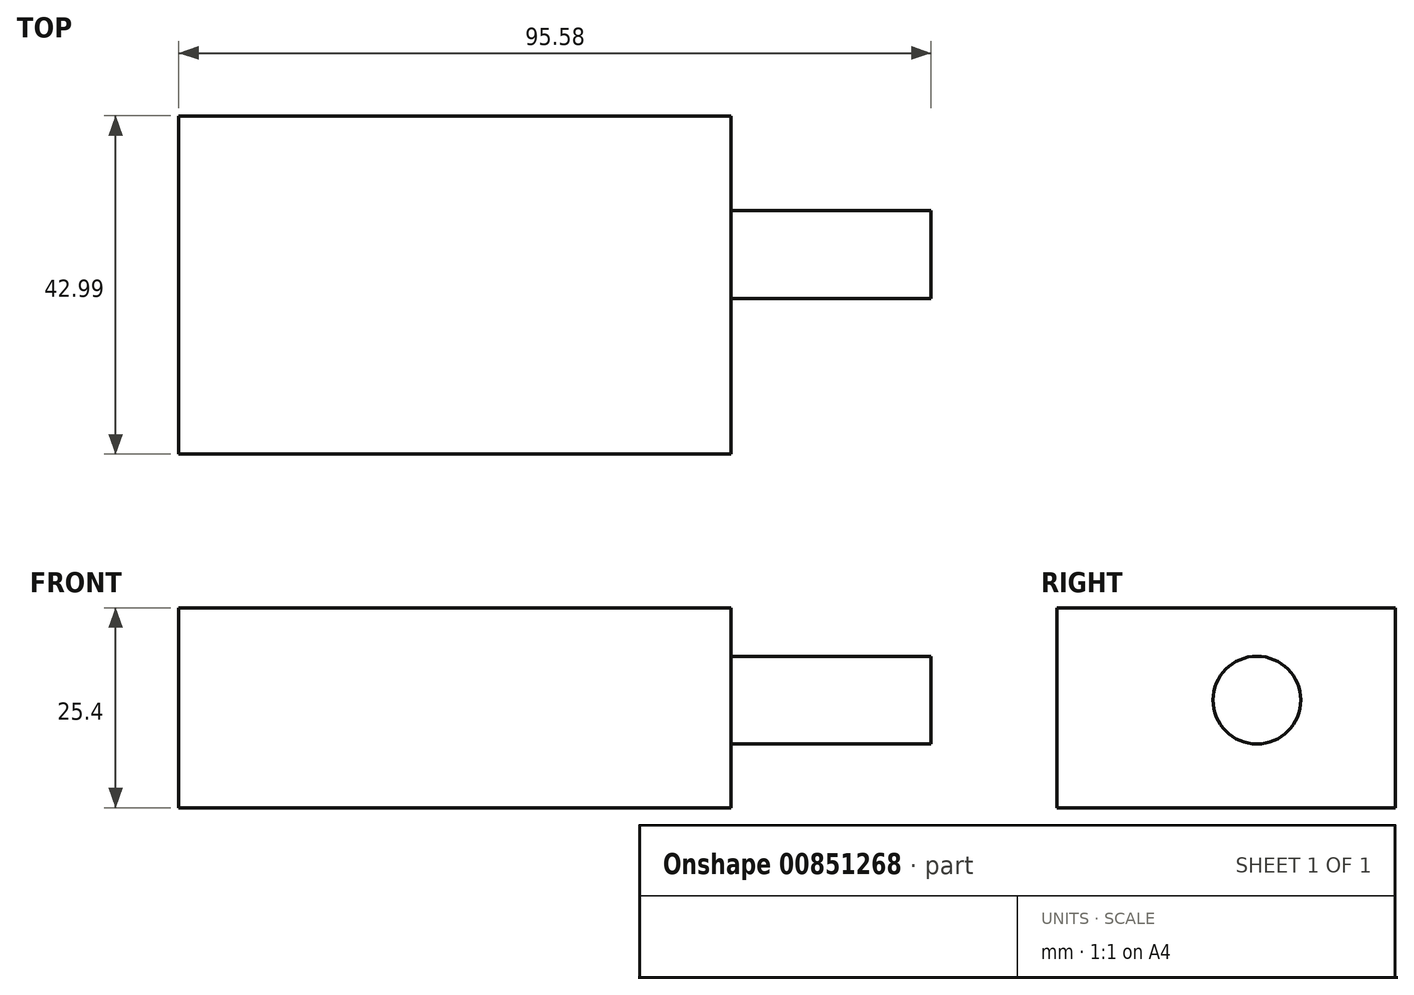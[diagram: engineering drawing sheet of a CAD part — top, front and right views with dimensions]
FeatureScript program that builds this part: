
annotation { "Feature Type Name" : "Feature", "Feature Type Description" : "" }
export const myFeature = defineFeature(function(context is Context, id is Id, definition is map)
    precondition{}
    {
        {
            var Q0;
            Q0=qCreatedBy(makeId("Top.planeOp"),FACE);
            var sketch = newSketch(context, id + "F0", { "sketchPlane" : qUnion([Q0])});
            skLineSegment(sketch, "E0.bottom", {"start": v(0, 0) * mm, "end": v(70.18, 0) * mm});
            skLineSegment(sketch, "E0.top", {"start": v(0, 42.99) * mm, "end": v(70.18, 42.99) * mm});
            skLineSegment(sketch, "E0.left", {"start": v(0, 0) * mm, "end": v(0, 42.99) * mm});
            skLineSegment(sketch, "E0.right", {"start": v(70.18, 0) * mm, "end": v(70.18, 42.99) * mm});
            skSolve(sketch);
        }
        {
            var Q0;
            Q0=makeQuery(id+"F0.imprint","IMPRINT",FACE,{"disambiguationData":[TD([[makeQuery(id+"F0.imprint","IMPRINT",EDGE,{"derivedFrom":sQuery(id+"F0.wireOp",EDGE,"E0.bottom")}),1.0]])]});
            extrude(context, id + "F1", {"entities" : qUnion([Q0]), "depth" : 25.4 * mm, "offsetDistance" : 25.4 * mm});
        }
        {
            var Q0;
            Q0=makeQuery(id+"F1.opExtrude","SWEPT_FACE",FACE,{"disambiguationData":[OSD([sQuery(id+"F0.wireOp",EDGE,"E0.right")])]});
            var sketch = newSketch(context, id + "F2", { "sketchPlane" : qUnion([Q0])});
            skCircle(sketch, "E1", {"center": v(25.38, 13.66) * mm, "radius": 5.57 * mm});
            skSolve(sketch);
        }
        {
            var Q0;
            Q0=makeQuery(id+"F2.imprint","IMPRINT",FACE,{"disambiguationData":[TD([[makeQuery(id+"F2.imprint","IMPRINT",EDGE,{"derivedFrom":sQuery(id+"F2.wireOp",EDGE,"E1")}),1.0]])]});
            extrude(context, id + "F3", {"entities" : qUnion([Q0]), "operationType" : NewBodyOperationType.ADD, "depth" : 25.4 * mm, "offsetDistance" : 25.4 * mm});
        }
    });
